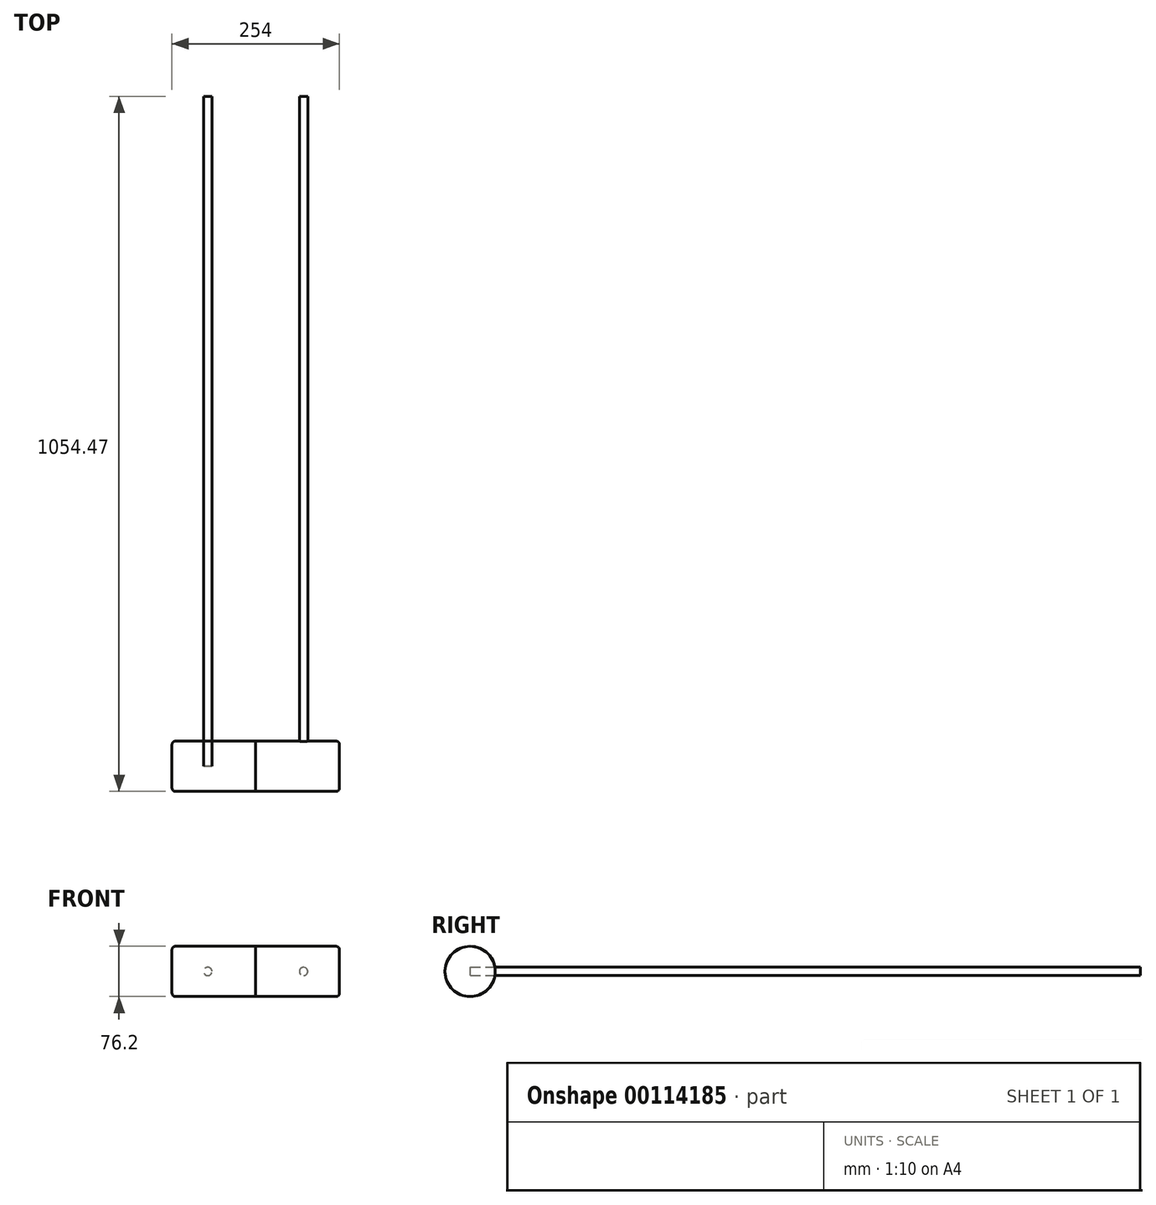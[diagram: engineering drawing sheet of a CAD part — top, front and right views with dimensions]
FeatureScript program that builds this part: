
annotation { "Feature Type Name" : "Feature", "Feature Type Description" : "" }
export const myFeature = defineFeature(function(context is Context, id is Id, definition is map)
    precondition{}
    {
        {
            var Q0;
            Q0=qCreatedBy(makeId("Front.planeOp"),FACE);
            var sketch = newSketch(context, id + "F0", { "sketchPlane" : qUnion([Q0])});
            skCircle(sketch, "E0", {"center": v(-72.75, 0) * mm, "radius": 6.35 * mm});
            skCircle(sketch, "E1", {"center": v(72.47, 0) * mm, "radius": 6.35 * mm});
            skSolve(sketch);
        }
        {
            var Q0;
            Q0=makeQuery(id+"F0.imprint","IMPRINT",FACE,{"disambiguationData":[TD([[makeQuery(id+"F0.imprint","IMPRINT",EDGE,{"derivedFrom":sQuery(id+"F0.wireOp",EDGE,"E1")}),1.0]])]});
            var Q1;
            Q1=makeQuery(id+"F0.imprint","IMPRINT",FACE,{"disambiguationData":[TD([[makeQuery(id+"F0.imprint","IMPRINT",EDGE,{"derivedFrom":sQuery(id+"F0.wireOp",EDGE,"E0")}),1.0]])]});
            extrude(context, id + "F1", {"entities" : qUnion([Q0, Q1]), "depth" : 1016 * mm});
        }
        {
            var Q0;
            Q0=qCreatedBy(makeId("Right.planeOp"),FACE);
            var sketch = newSketch(context, id + "F2", { "sketchPlane" : qUnion([Q0])});
            skCircle(sketch, "E2", {"center": v(-1016.37, 0) * mm, "radius": 38.1 * mm});
            skSolve(sketch);
        }
        {
            var Q0;
            Q0=makeQuery(id+"F2.imprint","IMPRINT",FACE,{"disambiguationData":[TD([[makeQuery(id+"F2.imprint","IMPRINT",EDGE,{"derivedFrom":sQuery(id+"F2.wireOp",EDGE,"E2")}),1.0]])]});
            extrude(context, id + "F3", {"entities" : qUnion([Q0]), "operationType" : NewBodyOperationType.ADD, "depth" : 127 * mm});
        }
        {
            var Q0;
            Q0=makeQuery(id+"F3.opExtrude","CAP_FACE",FACE,{"disambiguationData":[OSD([sQuery(id+"F2.wireOp",EDGE,"E2")])],"isStart":true});
            extrude(context, id + "F4", {"entities" : qUnion([Q0]), "depth" : 127 * mm});
        }
        {
            var Q0;
            Q0=makeQuery(id+"F4.opExtrude","CAP_EDGE",EDGE,{"disambiguationData":[OSD([sQuery(id+"F2.wireOp",EDGE,"E2")])],"isStart":false});
            fillet(context, id + "F5", {"entities" : qUnion([Q0]), "radius" : 5.08 * mm, "tangentPropagation" : true, "allowEdgeOverflow" : false});
        }
        {
            var Q0;
            Q0=makeQuery(id+"F3.opExtrude","CAP_EDGE",EDGE,{"disambiguationData":[OSD([sQuery(id+"F2.wireOp",EDGE,"E2")])],"isStart":false});
            fillet(context, id + "F6", {"entities" : qUnion([Q0]), "radius" : 5.08 * mm, "tangentPropagation" : true, "allowEdgeOverflow" : false});
        }
    });
